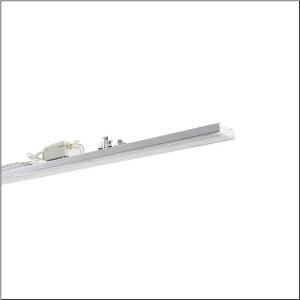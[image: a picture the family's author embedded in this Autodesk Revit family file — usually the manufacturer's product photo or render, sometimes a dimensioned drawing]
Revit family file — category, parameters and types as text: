
# Revit family: licross_r__21_recessed_ho_52tl11cn4c5s_2da8
name_source: partatom
category: Lighting Fixtures
units: mm (PartAtom-declared; Revit-internal decimal feet)

## family parameters
Cut with Voids When Loaded = No
Host = Face
Light Source = No
Part Type = Normal
Room Calculation Point = No
Round Connector Dimension = Use Diameter
Shared = No

## types (1)
- --- (1 x LED, 12640 lm, 68.4 W, 4000K)
    Apparent Load = 68 VA
    CIE Flux Codes = 87 95 99 100 100
    Color Rendering = 80
    Color Temperature = 4000K
    Default Elevation = 1800 mm
    Description = Licross® 21 Recessed HO, luminaire insert, of sheet steel, galvanised, coil coated, white, length: 1.500mm, width: 66mm, height: 67mm, LED rated luminous flux: 12.640lm, light colour: 840, control gear: ON/OFF Multilumen, CLOi, control gear: ECG Multilumen, with plug, 3-pole, with phase selection, mains connection: 220..240V, AC, 50/60Hz, start of lifetime: 68W, end of service life: 83W, halogen-free wiring, primary light control with lens, of plastic, primary optical cover: cover, of PMMA, light emission: direct distribution, primary light characteristic: symmetric, protection rating (complete): IP40, insulation class (complete): insulation class I (protective earthing), certification: CE, ENEC, VDE, UKCA, protection symbol: D if used in an environment without relevant dust loads with corresponding accessories, impact resistance: IK06, permissible ambient temperature for indoor applications: -35..+30°C, corresponds to IFS (International Featured Standards) requirements for safety and quality in the food industry, reducing of maximum allowable ambient temperature of 5°C with ceiling mounting, LABS conformity tested according to VDMA 24364:2018-05, packaging unit: 1 piece
    Height = 58 mm
    Lamp = 1 x LED
    Lamp Light Flux = 12640 lm
    Lamp Power = 68.4 W
    Lamp count = 1
    Length = 1500 mm
    Luminous efficacy = 185 lm/W
    Manufacturer = Siteco
    ModVariant = No
    Model = 52TL11CN4C5S
    Mounting Place = Ceiling
    Mounting Type = Pendant
    Number of Poles = 1
    OnlyDefault = Yes
    Power Factor = 1
    Product Name = Licross® 21 Recessed HO
    Product group = luminaire insert
    ProductGroupID = 901
    Protection Class = Protection class I
    Protection Degree = IP 40
    RLX_Detail_Level = 1
    RLX_Emergency_Light_Flux = 0 lm
    RLX_Emergency_Type = 0
    RLX_Emergency_Type_DB = No
    RlxData = <blob elided: 22313 chars, md5=1959a996>
    Socket = socket
    Standby Power = 0 W
    System Light Flux = 12640 lm
    System Power = 68 W
    Type Comments = factory setting: luminous flux: 100 % | (A | C | E) | 161 mA
    Type Image = l_1296930.jpg
    URL = http://relux.com
    VarID = @adj_040801
    Voltage = 0 V
    Weight = 0.00 kg
    Width = 66 mm

## geometry (parser evidence)
native form markers: Blend x4, Sweep x11
no freeform markers — native parametric forms only
